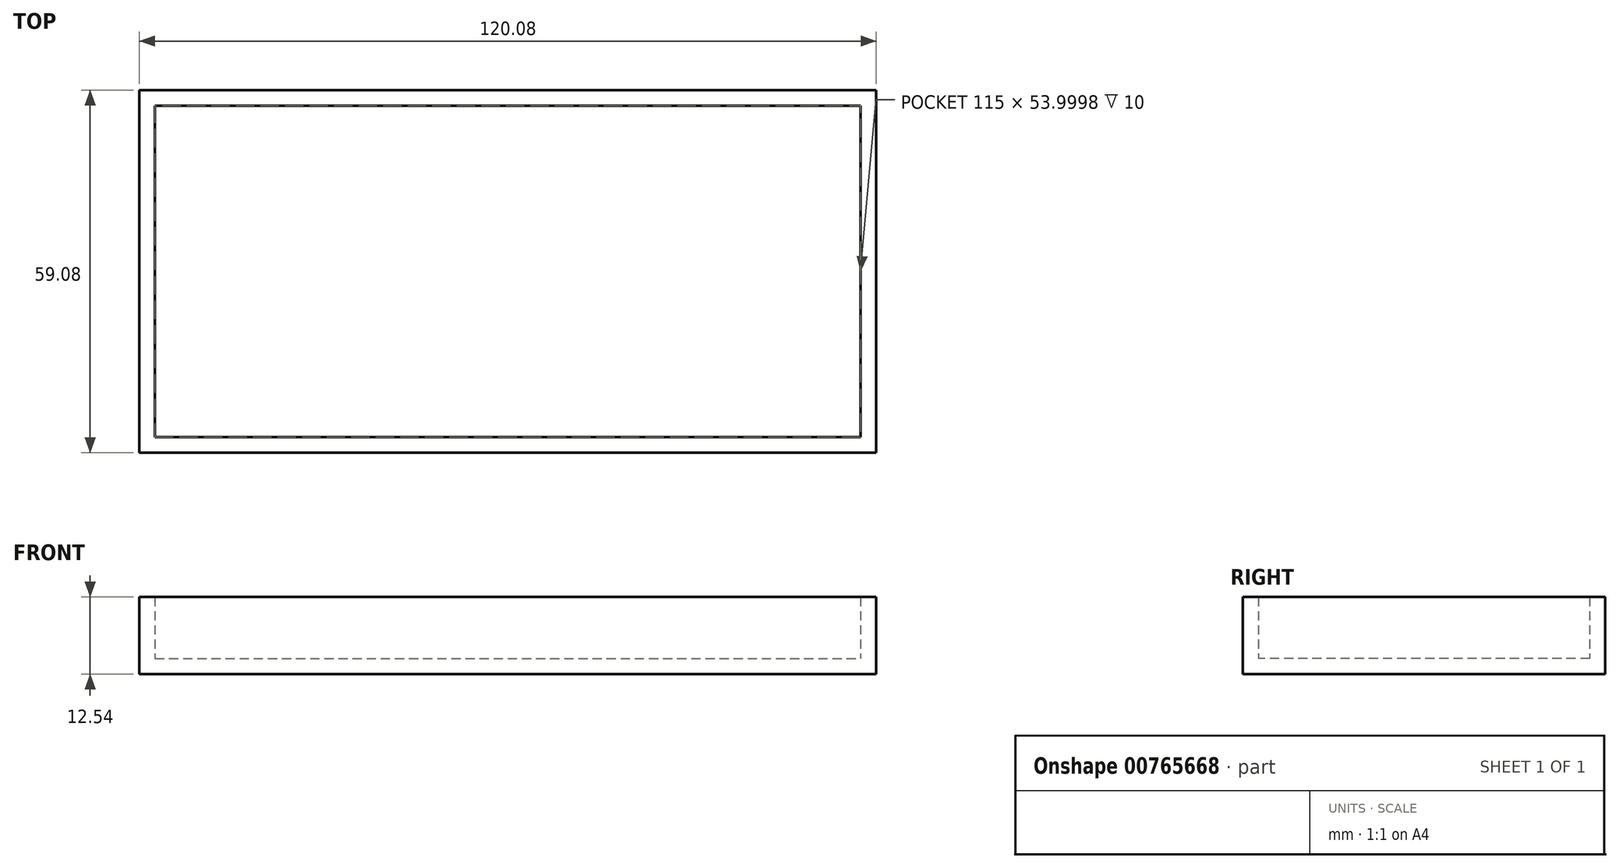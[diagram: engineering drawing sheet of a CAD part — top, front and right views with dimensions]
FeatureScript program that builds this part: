
annotation { "Feature Type Name" : "Feature", "Feature Type Description" : "" }
export const myFeature = defineFeature(function(context is Context, id is Id, definition is map)
    precondition{}
    {
        {
            var Q0;
            Q0=qCreatedBy(makeId("Top.planeOp"),FACE);
            var sketch = newSketch(context, id + "F0", { "sketchPlane" : qUnion([Q0])});
            skLineSegment(sketch, "E0.bottom", {"start": v(-50.8, 27.3) * mm, "end": v(64.2, 27.3) * mm});
            skLineSegment(sketch, "E0.top", {"start": v(-50.8, -26.7) * mm, "end": v(64.2, -26.7) * mm});
            skLineSegment(sketch, "E0.left", {"start": v(-50.8, 27.3) * mm, "end": v(-50.8, -26.7) * mm});
            skLineSegment(sketch, "E0.right", {"start": v(64.2, 27.3) * mm, "end": v(64.2, -26.7) * mm});
            skPoint(sketch, "E1", {"position": v(0, 0) * mm});
            skSolve(sketch);
        }
        {
            var Q0;
            Q0 = qSketchRegion(id + "F0", true);
            extrude(context, id + "F1", {"entities" : qUnion([Q0]), "depth" : 10 * mm, "offsetDistance" : 25.4 * mm});
        }
        {
            var Q0;
            Q0=makeQuery(id+"F1.opExtrude","CAP_FACE",FACE,{"disambiguationData":[OSD([sQuery(id+"F0.wireOp",EDGE,"E0.bottom"),sQuery(id+"F0.wireOp",EDGE,"E0.top"),sQuery(id+"F0.wireOp",EDGE,"E0.left"),sQuery(id+"F0.wireOp",EDGE,"E0.right")])],"isStart":false});
            shell(context, id + "F2", {"entities" : qUnion([Q0]), "thickness" : 2.54 * mm, "oppositeDirection" : true});
        }
    });
